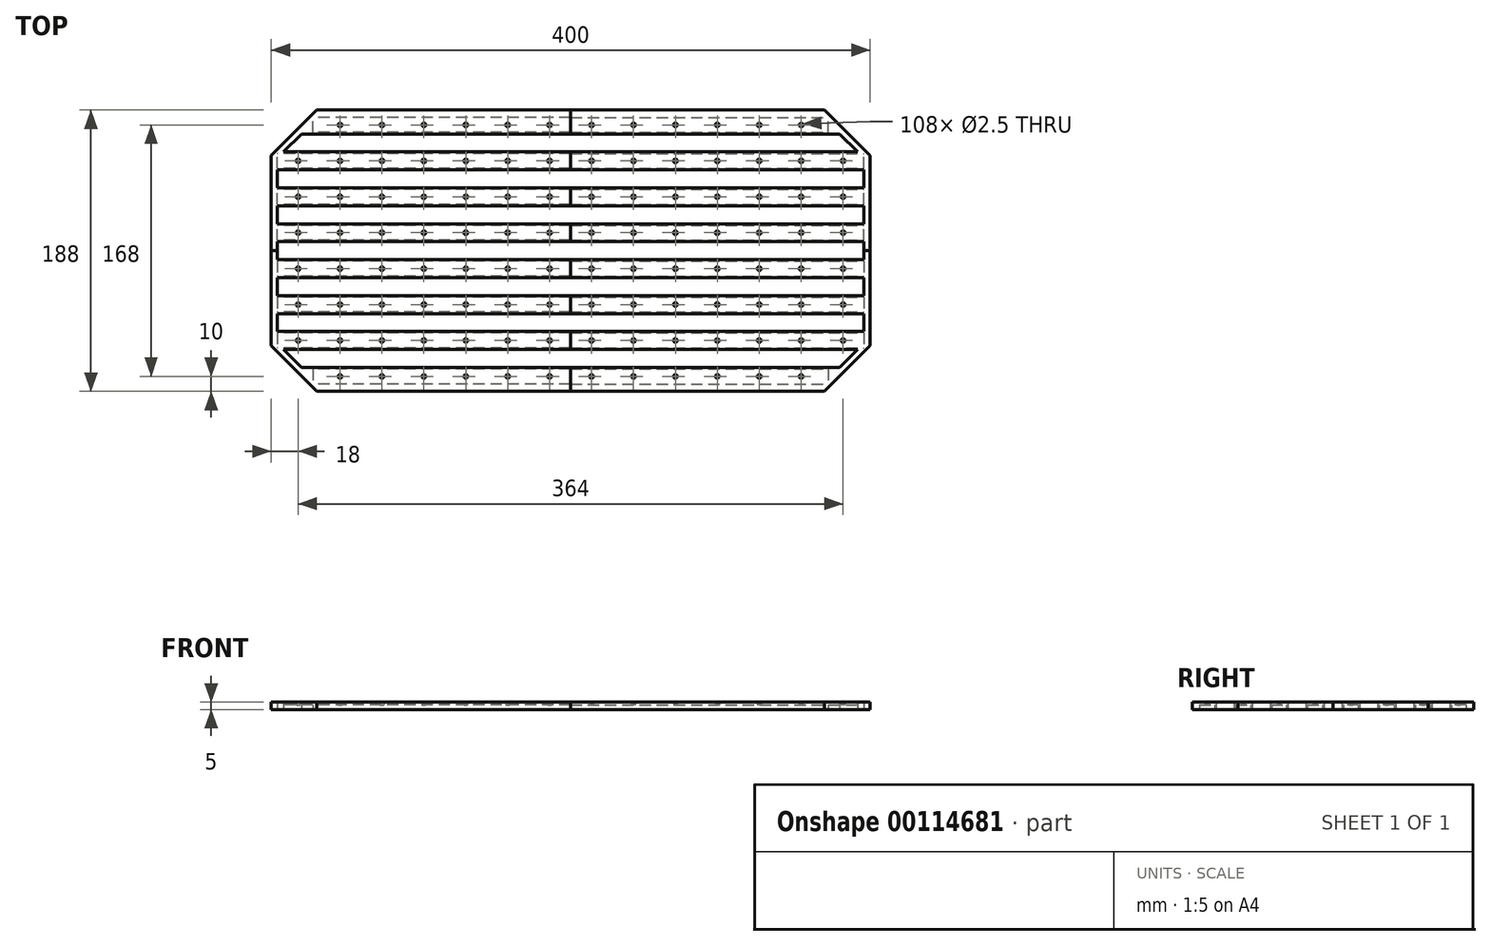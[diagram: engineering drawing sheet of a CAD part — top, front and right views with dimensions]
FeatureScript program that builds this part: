
annotation { "Feature Type Name" : "Feature", "Feature Type Description" : "" }
export const myFeature = defineFeature(function(context is Context, id is Id, definition is map)
    precondition{}
    {
        {
            var Q0;
            Q0=qCreatedBy(makeId("Top.planeOp"),FACE);
            var sketch = newSketch(context, id + "F0", { "sketchPlane" : qUnion([Q0])});
            skLineSegment(sketch, "E0", {"start": v(-169.5, 94) * mm, "end": v(0, 94) * mm});
            skLineSegment(sketch, "E1", {"start": v(0, 94) * mm, "end": v(0, 0) * mm});
            skLineSegment(sketch, "E2", {"start": v(0, 0) * mm, "end": v(-200, 0) * mm});
            skLineSegment(sketch, "E3", {"start": v(-200, 0) * mm, "end": v(-200, 63.5) * mm});
            skLineSegment(sketch, "E4", {"start": v(-200, 63.5) * mm, "end": v(-169.5, 94) * mm});
            skLineSegment(sketch, "E5.0", {"start": v(-167.84, 90) * mm, "end": v(0, 90) * mm});
            skLineSegment(sketch, "E5.1", {"start": v(-196, 61.84) * mm, "end": v(-167.84, 90) * mm});
            skLineSegment(sketch, "E5.2", {"start": v(-196, 0) * mm, "end": v(-196, 61.84) * mm});
            skLineSegment(sketch, "E6.bottom", {"start": v(-196, 6) * mm, "end": v(0, 6) * mm});
            skLineSegment(sketch, "E7.0.1.0", {"start": v(-196, 18) * mm, "end": v(0, 18) * mm});
            skLineSegment(sketch, "E7.0.2.0", {"start": v(-196, 30) * mm, "end": v(0, 30) * mm});
            skLineSegment(sketch, "E7.0.3.0", {"start": v(-196, 42) * mm, "end": v(0, 42) * mm});
            skLineSegment(sketch, "E7.0.4.0", {"start": v(-196, 54) * mm, "end": v(0, 54) * mm});
            skLineSegment(sketch, "E7.0.5.0", {"start": v(-191.84, 66) * mm, "end": v(0, 66) * mm});
            skLineSegment(sketch, "E7.0.6.0", {"start": v(-179.84, 78) * mm, "end": v(0, 78) * mm});
            skLineSegment(sketch, "E7.direction1", {"start": v(-196, 6) * mm, "end": v(-171, 6) * mm, "construction": true});
            skLineSegment(sketch, "E7.direction2", {"start": v(-196, 6) * mm, "end": v(-196, 18) * mm, "construction": true});
            skSolve(sketch);
        }
        {
            var Q0;
            {var subQ0=sQuery(id+"F0.wireOp",EDGE,"E5.0");Q0=makeQuery(id+"F0.imprint","IMPRINT",FACE,{"disambiguationData":[TD([[makeQuery(id+"F0.imprint","IMPRINT",EDGE,{"derivedFrom":subQ0}),-1.0]])]});}
            var Q1;
            {var subQ3=sQuery(id+"F0.wireOp",EDGE,"E7.0.4.0");Q1=makeQuery(id+"F0.imprint","IMPRINT",FACE,{"disambiguationData":[TD([[makeQuery(id+"F0.imprint","IMPRINT",EDGE,{"derivedFrom":subQ3}),1.0]])]});}
            var Q2;
            {var subQ0=sQuery(id+"F0.wireOp",EDGE,"E7.0.2.0");Q2=makeQuery(id+"F0.imprint","IMPRINT",FACE,{"disambiguationData":[TD([[makeQuery(id+"F0.imprint","IMPRINT",EDGE,{"derivedFrom":subQ0}),1.0]])]});}
            var Q3;
            {var subQ0=sQuery(id+"F0.wireOp",EDGE,"E6.bottom");Q3=makeQuery(id+"F0.imprint","IMPRINT",FACE,{"disambiguationData":[TD([[makeQuery(id+"F0.imprint","IMPRINT",EDGE,{"derivedFrom":subQ0}),1.0]])]});}
            var Q4;
            {var subQ14=sQuery(id+"F0.wireOp",EDGE,"E0");Q4=makeQuery(id+"F0.imprint","IMPRINT",FACE,{"disambiguationData":[TD([[makeQuery(id+"F0.imprint","IMPRINT",EDGE,{"derivedFrom":subQ14}),-1.0]])]});}
            extrude(context, id + "F1", {"entities" : qUnion([Q0, Q1, Q2, Q3, Q4]), "depth" : 5 * mm});
        }
        {
            var Q0;
            Q0=makeQuery(id+"F1.opExtrude","CAP_FACE",FACE,{"disambiguationData":[OSD([sQuery(id+"F0.wireOp",EDGE,"E0"),sQuery(id+"F0.wireOp",EDGE,"E1"),sQuery(id+"F0.wireOp",EDGE,"E2"),sQuery(id+"F0.wireOp",EDGE,"E3"),sQuery(id+"F0.wireOp",EDGE,"E4"),sQuery(id+"F0.wireOp",EDGE,"E5.1"),sQuery(id+"F0.wireOp",EDGE,"E5.2"),sQuery(id+"F0.wireOp",EDGE,"E6.bottom"),sQuery(id+"F0.wireOp",EDGE,"E7.0.1.0"),sQuery(id+"F0.wireOp",EDGE,"E7.0.2.0"),sQuery(id+"F0.wireOp",EDGE,"E7.0.3.0"),sQuery(id+"F0.wireOp",EDGE,"E7.0.4.0"),sQuery(id+"F0.wireOp",EDGE,"E7.0.5.0"),sQuery(id+"F0.wireOp",EDGE,"E7.0.6.0")])],"isStart":true});
            var sketch = newSketch(context, id + "F2", { "sketchPlane" : qUnion([Q0])});
            skLineSegment(sketch, "E8.bottom", {"start": v(0, -79) * mm, "end": v(-172, -79) * mm});
            skLineSegment(sketch, "E8.top", {"start": v(0, -89) * mm, "end": v(-172, -89) * mm});
            skLineSegment(sketch, "E8.left", {"start": v(0, -79) * mm, "end": v(0, -89) * mm});
            skLineSegment(sketch, "E8.right", {"start": v(-172, -79) * mm, "end": v(-172, -89) * mm});
            skLineSegment(sketch, "E9.bottom", {"start": v(0, -55) * mm, "end": v(-196, -55) * mm});
            skLineSegment(sketch, "E9.top", {"start": v(0, -65) * mm, "end": v(-196, -65) * mm});
            skLineSegment(sketch, "E9.left", {"start": v(0, -55) * mm, "end": v(0, -65) * mm});
            skLineSegment(sketch, "E9.right", {"start": v(-196, -55) * mm, "end": v(-196, -65) * mm});
            skLineSegment(sketch, "E10.bottom", {"start": v(0, -31) * mm, "end": v(-196, -31) * mm});
            skLineSegment(sketch, "E10.top", {"start": v(0, -41) * mm, "end": v(-196, -41) * mm});
            skLineSegment(sketch, "E10.left", {"start": v(0, -31) * mm, "end": v(0, -41) * mm});
            skLineSegment(sketch, "E10.right", {"start": v(-196, -31) * mm, "end": v(-196, -41) * mm});
            skLineSegment(sketch, "E11.bottom", {"start": v(0, -7) * mm, "end": v(-196, -7) * mm});
            skLineSegment(sketch, "E11.top", {"start": v(0, -17) * mm, "end": v(-196, -17) * mm});
            skLineSegment(sketch, "E11.left", {"start": v(0, -7) * mm, "end": v(0, -17) * mm});
            skLineSegment(sketch, "E11.right", {"start": v(-196, -7) * mm, "end": v(-196, -17) * mm});
            skLineSegment(sketch, "E12", {"start": v(-196, -60) * mm, "end": v(0, -60) * mm, "construction": true});
            skLineSegment(sketch, "E13", {"start": v(0, -36) * mm, "end": v(-196, -36) * mm, "construction": true});
            skLineSegment(sketch, "E14", {"start": v(-196, -12) * mm, "end": v(0, -12) * mm, "construction": true});
            skLineSegment(sketch, "E15", {"start": v(-197.25, -66.25) * mm, "end": v(-196, -65) * mm, "construction": true});
            skLineSegment(sketch, "E16", {"start": v(-173.25, -90.25) * mm, "end": v(-172, -89) * mm, "construction": true});
            skLineSegment(sketch, "E17.bottom", {"start": v(-196, -7) * mm, "end": v(-192.5, -7) * mm});
            skLineSegment(sketch, "E17.top", {"start": v(-196, -17) * mm, "end": v(-192.5, -17) * mm});
            skLineSegment(sketch, "E17.right", {"start": v(-192.5, -7) * mm, "end": v(-192.5, -17) * mm});
            skLineSegment(sketch, "E18.bottom", {"start": v(-196, -31) * mm, "end": v(-192.5, -31) * mm});
            skLineSegment(sketch, "E18.top", {"start": v(-196, -41) * mm, "end": v(-192.5, -41) * mm});
            skLineSegment(sketch, "E18.right", {"start": v(-192.5, -31) * mm, "end": v(-192.5, -41) * mm});
            skLineSegment(sketch, "E19.bottom", {"start": v(-196, -55) * mm, "end": v(-192.5, -55) * mm});
            skLineSegment(sketch, "E19.top", {"start": v(-196, -65) * mm, "end": v(-192.5, -65) * mm});
            skLineSegment(sketch, "E19.right", {"start": v(-192.5, -55) * mm, "end": v(-192.5, -65) * mm});
            skLineSegment(sketch, "E20.bottom", {"start": v(-172, -79) * mm, "end": v(-168.5, -79) * mm});
            skLineSegment(sketch, "E20.top", {"start": v(-172, -89) * mm, "end": v(-168.5, -89) * mm});
            skLineSegment(sketch, "E20.right", {"start": v(-168.5, -79) * mm, "end": v(-168.5, -89) * mm});
            skCircle(sketch, "E21", {"center": v(-14, -12) * mm, "radius": 1.25 * mm});
            skCircle(sketch, "E22.0.1.0", {"center": v(-14, -36) * mm, "radius": 1.25 * mm});
            skCircle(sketch, "E22.0.2.0", {"center": v(-14, -60) * mm, "radius": 1.25 * mm});
            skCircle(sketch, "E22.0.3.0", {"center": v(-14, -84) * mm, "radius": 1.25 * mm});
            skCircle(sketch, "E22.1.0.0", {"center": v(-42, -12) * mm, "radius": 1.25 * mm});
            skCircle(sketch, "E22.1.1.0", {"center": v(-42, -36) * mm, "radius": 1.25 * mm});
            skCircle(sketch, "E22.1.2.0", {"center": v(-42, -60) * mm, "radius": 1.25 * mm});
            skCircle(sketch, "E22.1.3.0", {"center": v(-42, -84) * mm, "radius": 1.25 * mm});
            skCircle(sketch, "E22.2.0.0", {"center": v(-70, -12) * mm, "radius": 1.25 * mm});
            skCircle(sketch, "E22.2.1.0", {"center": v(-70, -36) * mm, "radius": 1.25 * mm});
            skCircle(sketch, "E22.2.2.0", {"center": v(-70, -60) * mm, "radius": 1.25 * mm});
            skCircle(sketch, "E22.2.3.0", {"center": v(-70, -84) * mm, "radius": 1.25 * mm});
            skCircle(sketch, "E22.3.0.0", {"center": v(-98, -12) * mm, "radius": 1.25 * mm});
            skCircle(sketch, "E22.3.1.0", {"center": v(-98, -36) * mm, "radius": 1.25 * mm});
            skCircle(sketch, "E22.3.2.0", {"center": v(-98, -60) * mm, "radius": 1.25 * mm});
            skCircle(sketch, "E22.3.3.0", {"center": v(-98, -84) * mm, "radius": 1.25 * mm});
            skCircle(sketch, "E22.4.0.0", {"center": v(-126, -12) * mm, "radius": 1.25 * mm});
            skCircle(sketch, "E22.4.1.0", {"center": v(-126, -36) * mm, "radius": 1.25 * mm});
            skCircle(sketch, "E22.4.2.0", {"center": v(-126, -60) * mm, "radius": 1.25 * mm});
            skCircle(sketch, "E22.4.3.0", {"center": v(-126, -84) * mm, "radius": 1.25 * mm});
            skCircle(sketch, "E22.5.0.0", {"center": v(-154, -12) * mm, "radius": 1.25 * mm});
            skCircle(sketch, "E22.5.1.0", {"center": v(-154, -36) * mm, "radius": 1.25 * mm});
            skCircle(sketch, "E22.5.2.0", {"center": v(-154, -60) * mm, "radius": 1.25 * mm});
            skCircle(sketch, "E22.5.3.0", {"center": v(-154, -84) * mm, "radius": 1.25 * mm});
            skCircle(sketch, "E22.6.0.0", {"center": v(-182, -12) * mm, "radius": 1.25 * mm});
            skCircle(sketch, "E22.6.1.0", {"center": v(-182, -36) * mm, "radius": 1.25 * mm});
            skCircle(sketch, "E22.6.2.0", {"center": v(-182, -60) * mm, "radius": 1.25 * mm});
            skLineSegment(sketch, "E22.direction1", {"start": v(-14, -12) * mm, "end": v(-42, -12) * mm, "construction": true});
            skLineSegment(sketch, "E22.direction2", {"start": v(-14, -12) * mm, "end": v(-14, -36) * mm, "construction": true});
            skSolve(sketch);
        }
        {
            var Q0;
            Q0 = qSketchRegion(id + "F2", true);
            extrude(context, id + "F3", {"entities" : qUnion([Q0]), "operationType" : NewBodyOperationType.REMOVE, "oppositeDirection" : true, "depth" : 3 * mm});
        }
        {
            var Q0;
            Q0=makeQuery(id+"F2.imprint","IMPRINT",FACE,{"disambiguationData":[TD([[makeQuery(id+"F2.imprint","IMPRINT",EDGE,{"derivedFrom":sQuery(id+"F2.wireOp",EDGE,"E19.bottom")}),-1.0]])]});
            var Q1;
            Q1=makeQuery(id+"F2.imprint","IMPRINT",FACE,{"disambiguationData":[TD([[makeQuery(id+"F2.imprint","IMPRINT",EDGE,{"derivedFrom":sQuery(id+"F2.wireOp",EDGE,"E18.bottom")}),-1.0]])]});
            var Q2;
            Q2=makeQuery(id+"F2.imprint","IMPRINT",FACE,{"disambiguationData":[TD([[makeQuery(id+"F2.imprint","IMPRINT",EDGE,{"derivedFrom":sQuery(id+"F2.wireOp",EDGE,"E20.bottom")}),-1.0]])]});
            var Q3;
            Q3=makeQuery(id+"F2.imprint","IMPRINT",FACE,{"disambiguationData":[TD([[makeQuery(id+"F2.imprint","IMPRINT",EDGE,{"derivedFrom":sQuery(id+"F2.wireOp",EDGE,"E22.6.2.0")}),1.0]])]});
            var Q4;
            Q4=makeQuery(id+"F2.imprint","IMPRINT",FACE,{"disambiguationData":[TD([[makeQuery(id+"F2.imprint","IMPRINT",EDGE,{"derivedFrom":sQuery(id+"F2.wireOp",EDGE,"E22.5.2.0")}),1.0]])]});
            var Q5;
            Q5=makeQuery(id+"F2.imprint","IMPRINT",FACE,{"disambiguationData":[TD([[makeQuery(id+"F2.imprint","IMPRINT",EDGE,{"derivedFrom":sQuery(id+"F2.wireOp",EDGE,"E22.4.2.0")}),1.0]])]});
            var Q6;
            Q6=makeQuery(id+"F2.imprint","IMPRINT",FACE,{"disambiguationData":[TD([[makeQuery(id+"F2.imprint","IMPRINT",EDGE,{"derivedFrom":sQuery(id+"F2.wireOp",EDGE,"E22.3.2.0")}),1.0]])]});
            var Q7;
            Q7=makeQuery(id+"F2.imprint","IMPRINT",FACE,{"disambiguationData":[TD([[makeQuery(id+"F2.imprint","IMPRINT",EDGE,{"derivedFrom":sQuery(id+"F2.wireOp",EDGE,"E22.3.1.0")}),1.0]])]});
            var Q8;
            Q8=makeQuery(id+"F2.imprint","IMPRINT",FACE,{"disambiguationData":[TD([[makeQuery(id+"F2.imprint","IMPRINT",EDGE,{"derivedFrom":sQuery(id+"F2.wireOp",EDGE,"E22.4.1.0")}),1.0]])]});
            var Q9;
            Q9=makeQuery(id+"F2.imprint","IMPRINT",FACE,{"disambiguationData":[TD([[makeQuery(id+"F2.imprint","IMPRINT",EDGE,{"derivedFrom":sQuery(id+"F2.wireOp",EDGE,"E22.5.1.0")}),1.0]])]});
            var Q10;
            Q10=makeQuery(id+"F2.imprint","IMPRINT",FACE,{"disambiguationData":[TD([[makeQuery(id+"F2.imprint","IMPRINT",EDGE,{"derivedFrom":sQuery(id+"F2.wireOp",EDGE,"E22.5.0.0")}),1.0]])]});
            var Q11;
            Q11=makeQuery(id+"F2.imprint","IMPRINT",FACE,{"disambiguationData":[TD([[makeQuery(id+"F2.imprint","IMPRINT",EDGE,{"derivedFrom":sQuery(id+"F2.wireOp",EDGE,"E22.4.0.0")}),1.0]])]});
            var Q12;
            Q12=makeQuery(id+"F2.imprint","IMPRINT",FACE,{"disambiguationData":[TD([[makeQuery(id+"F2.imprint","IMPRINT",EDGE,{"derivedFrom":sQuery(id+"F2.wireOp",EDGE,"E22.3.0.0")}),1.0]])]});
            var Q13;
            Q13=makeQuery(id+"F2.imprint","IMPRINT",FACE,{"disambiguationData":[TD([[makeQuery(id+"F2.imprint","IMPRINT",EDGE,{"derivedFrom":sQuery(id+"F2.wireOp",EDGE,"E22.2.0.0")}),1.0]])]});
            var Q14;
            Q14=makeQuery(id+"F2.imprint","IMPRINT",FACE,{"disambiguationData":[TD([[makeQuery(id+"F2.imprint","IMPRINT",EDGE,{"derivedFrom":sQuery(id+"F2.wireOp",EDGE,"E22.1.0.0")}),1.0]])]});
            var Q15;
            Q15=makeQuery(id+"F2.imprint","IMPRINT",FACE,{"disambiguationData":[TD([[makeQuery(id+"F2.imprint","IMPRINT",EDGE,{"derivedFrom":sQuery(id+"F2.wireOp",EDGE,"E22.1.1.0")}),1.0]])]});
            var Q16;
            Q16=makeQuery(id+"F2.imprint","IMPRINT",FACE,{"disambiguationData":[TD([[makeQuery(id+"F2.imprint","IMPRINT",EDGE,{"derivedFrom":sQuery(id+"F2.wireOp",EDGE,"E22.2.1.0")}),1.0]])]});
            var Q17;
            Q17=makeQuery(id+"F2.imprint","IMPRINT",FACE,{"disambiguationData":[TD([[makeQuery(id+"F2.imprint","IMPRINT",EDGE,{"derivedFrom":sQuery(id+"F2.wireOp",EDGE,"E22.2.2.0")}),1.0]])]});
            var Q18;
            Q18=makeQuery(id+"F2.imprint","IMPRINT",FACE,{"disambiguationData":[TD([[makeQuery(id+"F2.imprint","IMPRINT",EDGE,{"derivedFrom":sQuery(id+"F2.wireOp",EDGE,"E22.1.2.0")}),1.0]])]});
            var Q19;
            Q19=makeQuery(id+"F2.imprint","IMPRINT",FACE,{"disambiguationData":[TD([[makeQuery(id+"F2.imprint","IMPRINT",EDGE,{"derivedFrom":sQuery(id+"F2.wireOp",EDGE,"E22.6.1.0")}),1.0]])]});
            var Q20;
            Q20=makeQuery(id+"F2.imprint","IMPRINT",FACE,{"disambiguationData":[TD([[makeQuery(id+"F2.imprint","IMPRINT",EDGE,{"derivedFrom":sQuery(id+"F2.wireOp",EDGE,"E22.6.0.0")}),1.0]])]});
            var Q21;
            Q21=makeQuery(id+"F2.imprint","IMPRINT",FACE,{"disambiguationData":[TD([[makeQuery(id+"F2.imprint","IMPRINT",EDGE,{"derivedFrom":sQuery(id+"F2.wireOp",EDGE,"E22.5.3.0")}),1.0]])]});
            var Q22;
            Q22=makeQuery(id+"F2.imprint","IMPRINT",FACE,{"disambiguationData":[TD([[makeQuery(id+"F2.imprint","IMPRINT",EDGE,{"derivedFrom":sQuery(id+"F2.wireOp",EDGE,"E22.4.3.0")}),1.0]])]});
            var Q23;
            Q23=makeQuery(id+"F2.imprint","IMPRINT",FACE,{"disambiguationData":[TD([[makeQuery(id+"F2.imprint","IMPRINT",EDGE,{"derivedFrom":sQuery(id+"F2.wireOp",EDGE,"E22.3.3.0")}),1.0]])]});
            var Q24;
            Q24=makeQuery(id+"F2.imprint","IMPRINT",FACE,{"disambiguationData":[TD([[makeQuery(id+"F2.imprint","IMPRINT",EDGE,{"derivedFrom":sQuery(id+"F2.wireOp",EDGE,"E22.2.3.0")}),1.0]])]});
            var Q25;
            Q25=makeQuery(id+"F2.imprint","IMPRINT",FACE,{"disambiguationData":[TD([[makeQuery(id+"F2.imprint","IMPRINT",EDGE,{"derivedFrom":sQuery(id+"F2.wireOp",EDGE,"E22.1.3.0")}),1.0]])]});
            var Q26;
            Q26=makeQuery(id+"F2.imprint","IMPRINT",FACE,{"disambiguationData":[TD([[makeQuery(id+"F2.imprint","IMPRINT",EDGE,{"derivedFrom":sQuery(id+"F2.wireOp",EDGE,"E22.0.3.0")}),1.0]])]});
            var Q27;
            Q27=makeQuery(id+"F2.imprint","IMPRINT",FACE,{"disambiguationData":[TD([[makeQuery(id+"F2.imprint","IMPRINT",EDGE,{"derivedFrom":sQuery(id+"F2.wireOp",EDGE,"E22.0.2.0")}),1.0]])]});
            var Q28;
            Q28=makeQuery(id+"F2.imprint","IMPRINT",FACE,{"disambiguationData":[TD([[makeQuery(id+"F2.imprint","IMPRINT",EDGE,{"derivedFrom":sQuery(id+"F2.wireOp",EDGE,"E22.0.1.0")}),1.0]])]});
            var Q29;
            Q29=makeQuery(id+"F2.imprint","IMPRINT",FACE,{"disambiguationData":[TD([[makeQuery(id+"F2.imprint","IMPRINT",EDGE,{"derivedFrom":sQuery(id+"F2.wireOp",EDGE,"E21")}),1.0]])]});
            var Q30;
            Q30=makeQuery(id+"F2.imprint","IMPRINT",FACE,{"disambiguationData":[TD([[makeQuery(id+"F2.imprint","IMPRINT",EDGE,{"derivedFrom":sQuery(id+"F2.wireOp",EDGE,"E17.bottom")}),-1.0]])]});
            extrude(context, id + "F4", {"entities" : qUnion([Q0, Q1, Q2, Q3, Q4, Q5, Q6, Q7, Q8, Q9, Q10, Q11, Q12, Q13, Q14, Q15, Q16, Q17, Q18, Q19, Q20, Q21, Q22, Q23, Q24, Q25, Q26, Q27, Q28, Q29, Q30]), "operationType" : NewBodyOperationType.REMOVE, "endBound" : BoundingType.THROUGH_ALL, "oppositeDirection" : true, "depth" : 25 * mm});
        }
        {
            var Q0;
            Q0=makeQuery(id+"F1.opExtrude","SWEPT_BODY",BODY,{"disambiguationData":[OSD([sQuery(id+"F0.wireOp",EDGE,"E0"),sQuery(id+"F0.wireOp",EDGE,"E1"),sQuery(id+"F0.wireOp",EDGE,"E2"),sQuery(id+"F0.wireOp",EDGE,"E3"),sQuery(id+"F0.wireOp",EDGE,"E4"),sQuery(id+"F0.wireOp",EDGE,"E5.1"),sQuery(id+"F0.wireOp",EDGE,"E5.2"),sQuery(id+"F0.wireOp",EDGE,"E6.bottom"),sQuery(id+"F0.wireOp",EDGE,"E7.0.1.0"),sQuery(id+"F0.wireOp",EDGE,"E7.0.2.0"),sQuery(id+"F0.wireOp",EDGE,"E7.0.3.0"),sQuery(id+"F0.wireOp",EDGE,"E7.0.4.0"),sQuery(id+"F0.wireOp",EDGE,"E7.0.5.0"),sQuery(id+"F0.wireOp",EDGE,"E7.0.6.0")])]});
            var Q1;
            Q1=makeQuery(id+"F1.opExtrude","SWEPT_FACE",FACE,{"disambiguationData":[OSD([sQuery(id+"F0.wireOp",EDGE,"E2")])]});
            mirror(context, id + "F5", {"entities" : qUnion([Q0]), "mirrorPlane" : qUnion([Q1])});
        }
        {
            var Q0;
            Q0=makeQuery(id+"F1.opExtrude","SWEPT_BODY",BODY,{"disambiguationData":[OSD([sQuery(id+"F0.wireOp",EDGE,"E0"),sQuery(id+"F0.wireOp",EDGE,"E1"),sQuery(id+"F0.wireOp",EDGE,"E2"),sQuery(id+"F0.wireOp",EDGE,"E3"),sQuery(id+"F0.wireOp",EDGE,"E4"),sQuery(id+"F0.wireOp",EDGE,"E5.1"),sQuery(id+"F0.wireOp",EDGE,"E5.2"),sQuery(id+"F0.wireOp",EDGE,"E6.bottom"),sQuery(id+"F0.wireOp",EDGE,"E7.0.1.0"),sQuery(id+"F0.wireOp",EDGE,"E7.0.2.0"),sQuery(id+"F0.wireOp",EDGE,"E7.0.3.0"),sQuery(id+"F0.wireOp",EDGE,"E7.0.4.0"),sQuery(id+"F0.wireOp",EDGE,"E7.0.5.0"),sQuery(id+"F0.wireOp",EDGE,"E7.0.6.0")])]});
            var Q1;
            Q1=makeQuery(id+"F5.opPattern","COPY",BODY,{"derivedFrom":makeQuery(id+"F1.opExtrude","SWEPT_BODY",BODY,{"disambiguationData":[OSD([sQuery(id+"F0.wireOp",EDGE,"E0"),sQuery(id+"F0.wireOp",EDGE,"E1"),sQuery(id+"F0.wireOp",EDGE,"E2"),sQuery(id+"F0.wireOp",EDGE,"E3"),sQuery(id+"F0.wireOp",EDGE,"E4"),sQuery(id+"F0.wireOp",EDGE,"E5.1"),sQuery(id+"F0.wireOp",EDGE,"E5.2"),sQuery(id+"F0.wireOp",EDGE,"E6.bottom"),sQuery(id+"F0.wireOp",EDGE,"E7.0.1.0"),sQuery(id+"F0.wireOp",EDGE,"E7.0.2.0"),sQuery(id+"F0.wireOp",EDGE,"E7.0.3.0"),sQuery(id+"F0.wireOp",EDGE,"E7.0.4.0"),sQuery(id+"F0.wireOp",EDGE,"E7.0.5.0"),sQuery(id+"F0.wireOp",EDGE,"E7.0.6.0")])]}),"instanceName":"1"});
            var Q2;
            {var subQ0=sQuery(id+"F0.wireOp",EDGE,"E1");var subQ1=makeQuery(id+"F0.imprint","INTERSECT",VERTEX,{"derivedFrom":[subQ0,sQuery(id+"F0.wireOp",EDGE,"E5.0")]});Q2=makeQuery(id+"F5.opPattern","COPY",FACE,{"derivedFrom":makeQuery(id+"F1.opExtrude","SWEPT_FACE",FACE,{"disambiguationData":[OSD([subQ0]),TDD([makeQuery(id+"F0.imprint","IMPRINT",EDGE,{"disambiguationData":[TD([[makeQuery(id+"F0.imprint","INTERSECT",VERTEX,{"derivedFrom":[sQuery(id+"F0.wireOp",EDGE,"E0"),subQ0]}),-1.0]])],"derivedFrom":subQ0}),makeQuery(id+"F0.imprint","IMPRINT",EDGE,{"disambiguationData":[TD([[subQ1,-1.0]])],"derivedFrom":subQ0})])]}),"instanceName":"1"});}
            mirror(context, id + "F6", {"entities" : qUnion([Q0, Q1]), "mirrorPlane" : qUnion([Q2])});
        }
    });
